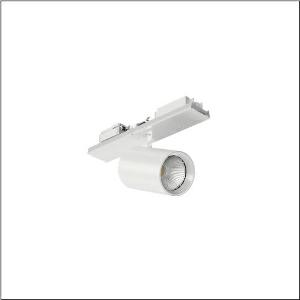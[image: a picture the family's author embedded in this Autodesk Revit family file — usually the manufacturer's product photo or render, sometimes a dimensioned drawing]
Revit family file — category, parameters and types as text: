
# Revit family: licross_r__spot_31_51sl137a43b_0799
name_source: partatom
category: Lighting Fixtures
units: mm (PartAtom-declared; Revit-internal decimal feet)

## family parameters
Cut with Voids When Loaded = No
Host = Face
Light Source = No
Part Type = Normal
Room Calculation Point = No
Round Connector Dimension = Use Diameter
Shared = No

## types (1)
- --- (1 x LED, 3680 lm, 28 W, 4000K)
    Apparent Load = 28 VA
    CIE Flux Codes = 92 97 99 100 100
    Color Rendering = 90
    Color Temperature = 4000K
    Default Elevation = 1800 mm
    Description = Licross® Spot 31, directional spotlight, light control with lens, of plastic, LED rated luminous flux: 3.680lm, light colour: 940, with plug, 3-pole, with phase selection, mains connection: 220..240V, AC, 50/60Hz, of aluminium, traffic white (RAL 9016), length: 300mm, diameter: 90mm, protection rating (complete): IP20, insulation class (complete): insulation class I (protective earthing), certification: CE, packaging unit: 1 piece
    Height = 175 mm
    Lamp = 1 x LED
    Lamp Light Flux = 3680 lm
    Lamp Power = 28 W
    Lamp count = 1
    Length = 90 mm
    Luminous efficacy = 131 lm/W
    Manufacturer = Siteco
    ModVariant = No
    Model = 51SL137A43B
    Mounting Place = Ceiling
    Mounting Type = Pendant
    Number of Poles = 1
    OnlyDefault = Yes
    Power Factor = 1
    Product Name = Licross® Spot 31
    Product group = directional spotlight
    ProductGroupID = 906
    Protection Class = Protection class I
    Protection Degree = IP 20
    RLX_Detail_Level = 1
    RLX_Emergency_Light_Flux = 0 lm
    RLX_Emergency_Type = 0
    RLX_Emergency_Type_DB = No
    RlxData = <blob elided: 14897 chars, md5=b602a8bc>
    Socket = socket
    Standby Power = 0 W
    System Light Flux = 3680 lm
    System Power = 28 W
    Type Comments = factory setting: luminous flux: 100 % | (ON | ON | ON) | 700 mA
    Type Image = l_1245720.jpg
    URL = http://relux.com
    VarID = @adj_127730
    Voltage = 0 V
    Weight = 0.00 kg
    Width = 0 mm  [stored 0 ft]

note: [stored X ft] marks values corroborated as IEEE doubles in the binary element streams (Revit-internal decimal feet)

## geometry (parser evidence)
native form markers: Sweep x13
no freeform markers — native parametric forms only
